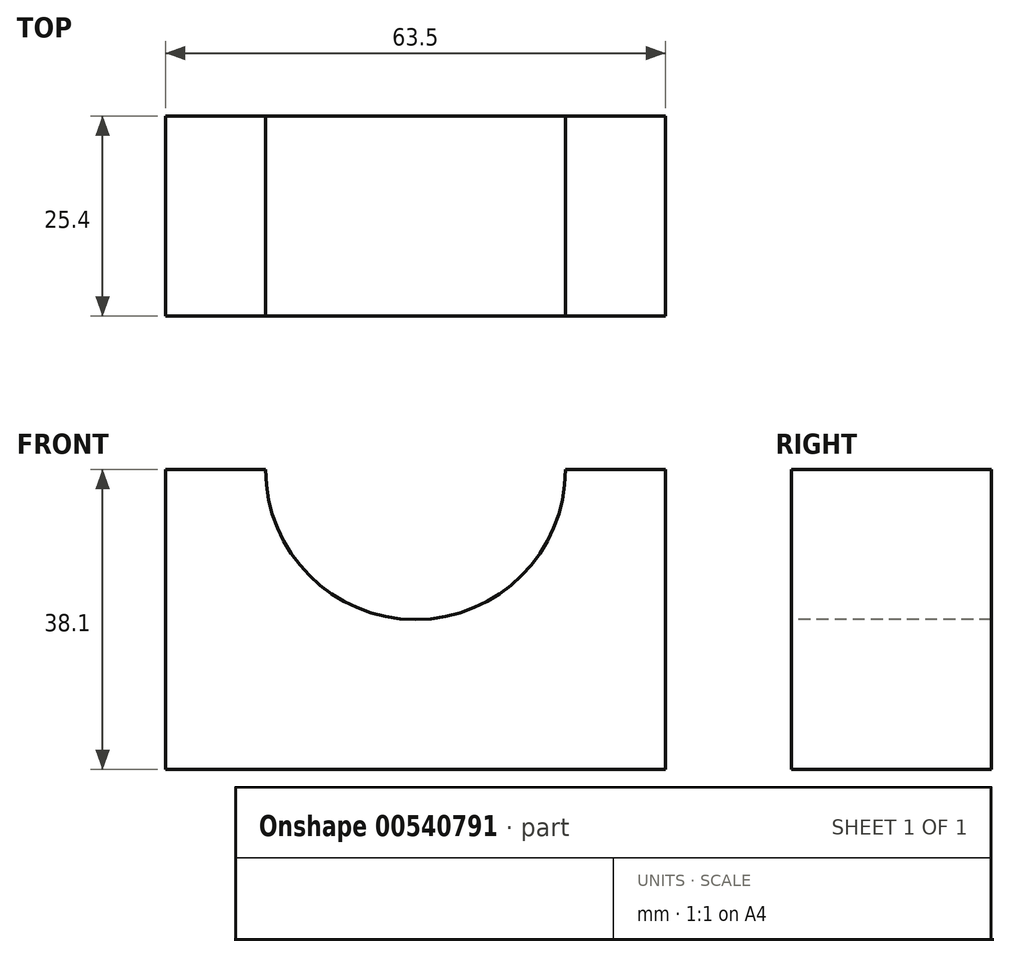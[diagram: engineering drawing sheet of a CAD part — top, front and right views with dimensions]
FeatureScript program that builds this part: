
annotation { "Feature Type Name" : "Feature", "Feature Type Description" : "" }
export const myFeature = defineFeature(function(context is Context, id is Id, definition is map)
    precondition{}
    {
        {
            var Q0;
            Q0=qCreatedBy(makeId("Front.planeOp"),FACE);
            var sketch = newSketch(context, id + "F0", { "sketchPlane" : qUnion([Q0])});
            skLineSegment(sketch, "E0", {"start": v(0, 0) * mm, "end": v(63.5, 0) * mm});
            skLineSegment(sketch, "E1", {"start": v(63.5, 0) * mm, "end": v(63.5, 38.1) * mm});
            skLineSegment(sketch, "E2", {"start": v(63.5, 38.1) * mm, "end": v(0, 38.1) * mm});
            skLineSegment(sketch, "E3", {"start": v(0, 38.1) * mm, "end": v(0, 0) * mm});
            skSolve(sketch);
        }
        {
            var Q0;
            Q0=makeQuery(id+"F0.imprint","IMPRINT",FACE,{"disambiguationData":[TD([[makeQuery(id+"F0.imprint","IMPRINT",EDGE,{"derivedFrom":sQuery(id+"F0.wireOp",EDGE,"E0")}),1.0]])]});
            extrude(context, id + "F1", {"entities" : qUnion([Q0]), "depth" : 25.4 * mm, "offsetDistance" : 25.4 * mm});
        }
        {
            var Q0;
            Q0=makeQuery(id+"F1.opExtrude","CAP_FACE",FACE,{"disambiguationData":[OSD([sQuery(id+"F0.wireOp",EDGE,"E0"),sQuery(id+"F0.wireOp",EDGE,"E1"),sQuery(id+"F0.wireOp",EDGE,"E2"),sQuery(id+"F0.wireOp",EDGE,"E3")])],"isStart":false});
            var sketch = newSketch(context, id + "F2", { "sketchPlane" : qUnion([Q0])});
            skCircle(sketch, "E4", {"center": v(31.75, 38.1) * mm, "radius": 19.05 * mm});
            skSolve(sketch);
        }
        {
            var Q0;
            {var subQ0=sQuery(id+"F2.wireOp",EDGE,"E4");var subQ1=makeQuery(id+"F1.opExtrude","CAP_EDGE",EDGE,{"disambiguationData":[OSD([sQuery(id+"F0.wireOp",EDGE,"E2")])],"isStart":false});var subQ2=makeQuery(id+"F2.imprint","INTERSECT",VERTEX,{"disambiguationData":[OD(0.0)],"derivedFrom":[subQ1,subQ0]});Q0=makeQuery(id+"F2.imprint","IMPRINT",FACE,{"disambiguationData":[TD([[makeQuery(id+"F2.imprint","IMPRINT",EDGE,{"disambiguationData":[TD([[subQ2,1.0]])],"derivedFrom":subQ0}),1.0]])]});}
            extrude(context, id + "F3", {"entities" : qUnion([Q0]), "operationType" : NewBodyOperationType.REMOVE, "oppositeDirection" : true, "depth" : 19.05 * mm, "offsetDistance" : 25.4 * mm});
        }
        {
            var Q0;
            Q0=makeQuery(id+"F3.boolean.opBoolean","COPY",FACE,{"derivedFrom":makeQuery(id+"F3.opExtrude","CAP_FACE",FACE,{"disambiguationData":[OSD([sQuery(id+"F0.wireOp",EDGE,"E2"),sQuery(id+"F2.wireOp",EDGE,"E4")])],"isStart":false})});
            extrude(context, id + "F4", {"entities" : qUnion([Q0]), "operationType" : NewBodyOperationType.REMOVE, "oppositeDirection" : true, "depth" : 19.05 * mm, "offsetDistance" : 25.4 * mm});
        }
    });
